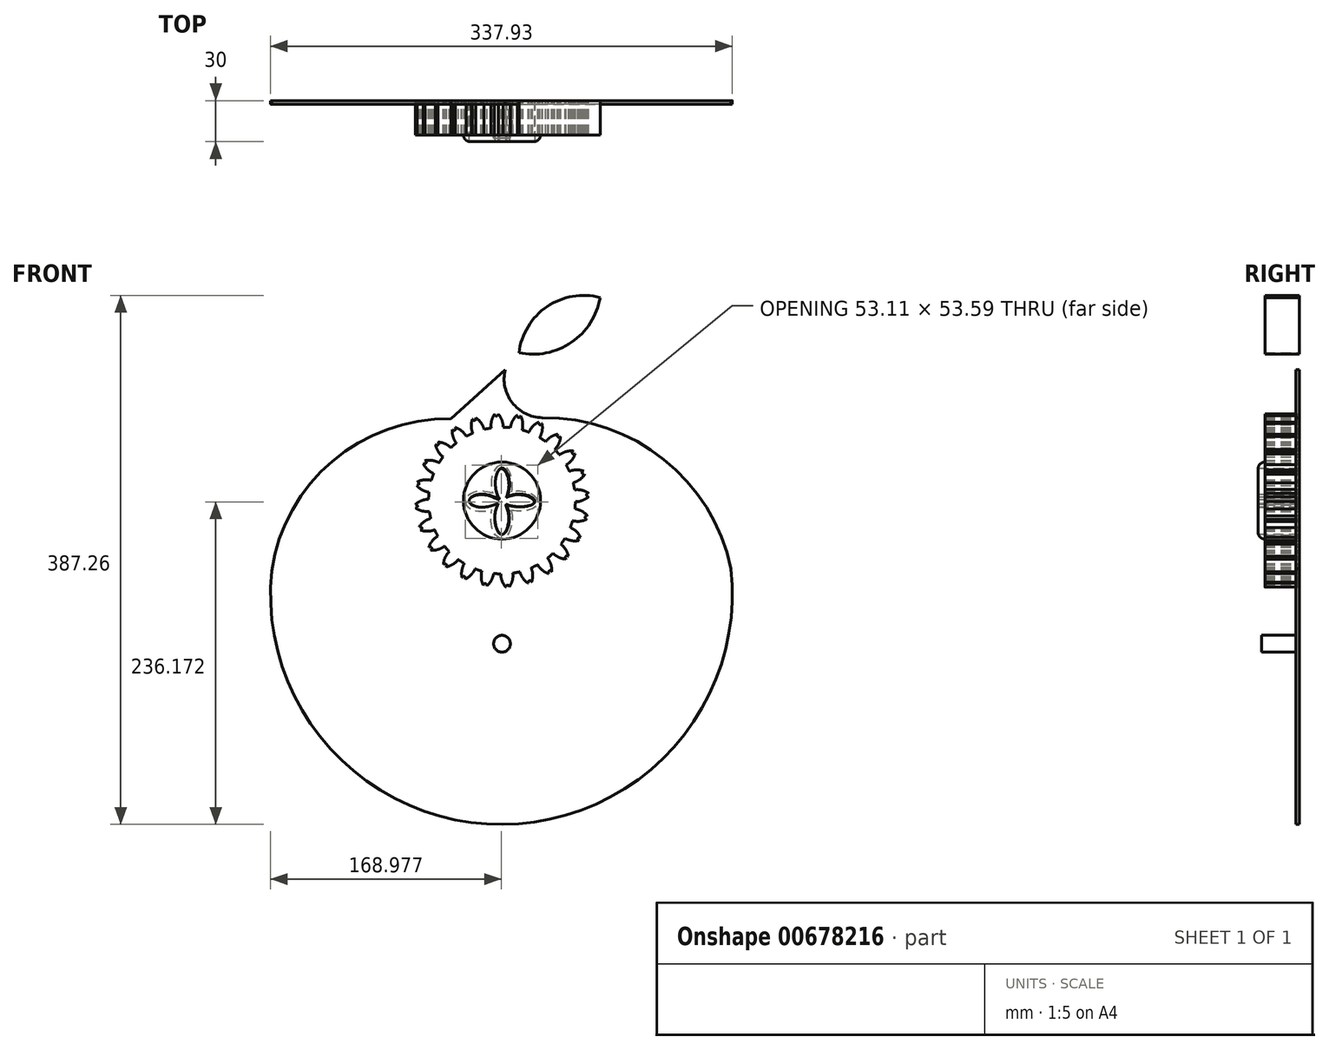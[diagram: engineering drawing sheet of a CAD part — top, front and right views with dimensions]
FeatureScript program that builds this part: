
annotation { "Feature Type Name" : "Feature", "Feature Type Description" : "" }
export const myFeature = defineFeature(function(context is Context, id is Id, definition is map)
    precondition{}
    {
        {
            var Q0;
            Q0=qCreatedBy(makeId("Front.planeOp"),FACE);
            var sketch = newSketch(context, id + "F0", { "sketchPlane" : qUnion([Q0])});
            skCircle(sketch, "E0", {"center": v(0, 0) * mm, "radius": 53.72 * mm});
            skCircle(sketch, "E1", {"center": v(0, 0) * mm, "radius": 58.67 * mm, "construction": true});
            skCircle(sketch, "E2", {"center": v(0, 0) * mm, "radius": 63.5 * mm, "construction": true});
            skLineSegment(sketch, "E3", {"start": v(0, 0) * mm, "end": v(0, 79.57) * mm, "construction": true});
            skLineSegment(sketch, "E4", {"start": v(0, 0) * mm, "end": v(-6.56, 100.09) * mm, "construction": true});
            skLineSegment(sketch, "E5", {"start": v(0, 58.67) * mm, "end": v(-52.8, 58.67) * mm, "construction": true});
            skLineSegment(sketch, "E6", {"start": v(0, 58.67) * mm, "end": v(-50.4, 40.33) * mm, "construction": true});
            skCircle(sketch, "E7", {"center": v(0, 0) * mm, "radius": 55.14 * mm, "construction": true});
            skCircle(sketch, "E8", {"center": v(0, 58.67) * mm, "radius": 14.6 * mm, "construction": true});
            skCircle(sketch, "E9", {"center": v(-13.72, 53.68) * mm, "radius": 14.6 * mm, "construction": true});
            skArc(sketch, "E10", {"start": v(0, 58.67) * mm, "mid": v(-1.2, 61.2) * mm, "end": v(-2.86, 63.44) * mm});
            skArc(sketch, "E11", {"start": v(0.88, 53.71) * mm, "mid": v(0.65, 56.23) * mm, "end": v(0, 58.67) * mm});
            skArc(sketch, "E12.MirrorCS", {"start": v(-7.66, 58.17) * mm, "mid": v(-6.8, 60.83) * mm, "end": v(-5.45, 63.27) * mm});
            skArc(sketch, "E13.MirrorCS", {"start": v(-7.88, 53.14) * mm, "mid": v(-7.99, 55.67) * mm, "end": v(-7.66, 58.17) * mm});
            skArc(sketch, "E14", {"start": v(-5.45, 63.27) * mm, "mid": v(-4.06, 61.88) * mm, "end": v(-2.86, 63.44) * mm});
            skCircle(sketch, "E15", {"center": v(0, 0) * mm, "radius": 28.21 * mm});
            skFitSpline(sketch, "E16", {"points": [v(0.41, -0.45) * mm, v(0, 0) * mm, v(-14.37, 4.8) * mm, v(-24, 0) * mm, v(-14.67, -4.85) * mm, v(0.41, -0.45) * mm]});
            skFitSpline(sketch, "E17", {"points": [v(0.41, -0.45) * mm, v(14.8, -4.52) * mm, v(24.13, -0.45) * mm, v(13.08, 4.76) * mm, v(0.41, -0.45) * mm]});
            skFitSpline(sketch, "E18", {"points": [v(0.41, -0.45) * mm, v(5.53, 12.84) * mm, v(0, 23.86) * mm, v(-4.88, 13.02) * mm, v(0.41, -0.45) * mm]});
            skFitSpline(sketch, "E19", {"points": [v(0, 0) * mm, v(5.4, -13.04) * mm, v(0, -24.75) * mm, v(-5.25, -13.1) * mm, v(0, 0) * mm]});
            skSolve(sketch);
        }
        {
            var Q0;
            {var subQ0=sQuery(id+"F0.wireOp",EDGE,"E0");var subQ1=makeQuery(id+"F0.imprint","INTERSECT",VERTEX,{"derivedFrom":[subQ0,sQuery(id+"F0.wireOp",EDGE,"E11")]});Q0=makeQuery(id+"F0.imprint","IMPRINT",FACE,{"disambiguationData":[TD([[makeQuery(id+"F0.imprint","IMPRINT",EDGE,{"disambiguationData":[TD([[subQ1,-1.0]])],"derivedFrom":subQ0}),1.0]])]});}
            var Q1;
            Q1=makeQuery(id+"F0.imprint","IMPRINT",FACE,{"disambiguationData":[TD([[makeQuery(id+"F0.imprint","IMPRINT",EDGE,{"derivedFrom":sQuery(id+"F0.wireOp",EDGE,"E10")}),1.0]])]});
            extrude(context, id + "F1", {"entities" : qUnion([Q0, Q1]), "depth" : 25 * mm, "offsetDistance" : 25 * mm});
        }
        {
            var Q0;
            Q0=makeQuery(id+"F1.opExtrude","SWEPT_BODY",BODY,{"disambiguationData":[OSD([sQuery(id+"F0.wireOp",EDGE,"E0"),sQuery(id+"F0.wireOp",EDGE,"E10"),sQuery(id+"F0.wireOp",EDGE,"E11"),sQuery(id+"F0.wireOp",EDGE,"E12.MirrorCS"),sQuery(id+"F0.wireOp",EDGE,"E13.MirrorCS"),sQuery(id+"F0.wireOp",EDGE,"E14")])]});
            var Q1;
            Q1=makeQuery(id+"F1.opExtrude","SWEPT_FACE",FACE,{"disambiguationData":[OSD([sQuery(id+"F0.wireOp",EDGE,"E0")])]});
            circularPattern(context, id + "F2", {"entities" : qUnion([Q0]), "axis" : qUnion([Q1]), "angle" : 360 * degree, "instanceCount" : 24, "equalSpace" : true});
        }
        {
            var Q0;
            Q0=makeQuery(id+"F0.imprint","IMPRINT",FACE,{"disambiguationData":[TD([[makeQuery(id+"F0.imprint","IMPRINT",EDGE,{"derivedFrom":sQuery(id+"F0.wireOp",EDGE,"E15")}),1.0]])]});
            extrude(context, id + "F3", {"entities" : qUnion([Q0]), "operationType" : NewBodyOperationType.ADD, "depth" : 30 * mm, "offsetDistance" : 25 * mm});
        }
        {
            var Q0;
            Q0=makeQuery(id+"F3.opExtrude","CAP_EDGE",EDGE,{"disambiguationData":[OSD([sQuery(id+"F0.wireOp",EDGE,"E15")])],"isStart":false});
            fillet(context, id + "F4", {"entities" : qUnion([Q0]), "radius" : 5 * mm, "tangentPropagation" : true, "allowEdgeOverflow" : false});
        }
        {
            var Q0;
            Q0=qCreatedBy(makeId("Front.planeOp"),FACE);
            var sketch = newSketch(context, id + "F5", { "sketchPlane" : qUnion([Q0])});
            skArc(sketch, "E20", {"start": v(-171.04, -51.27) * mm, "mid": v(0.49, -239.58) * mm, "end": v(170.05, -49.5) * mm});
            skArc(sketch, "E21", {"start": v(-38.25, 62.35) * mm, "mid": v(-125.97, 30.46) * mm, "end": v(-171.04, -51.27) * mm});
            skArc(sketch, "E22", {"start": v(170.05, -49.5) * mm, "mid": v(119.95, 32.07) * mm, "end": v(29.42, 63.16) * mm});
            skFitSpline(sketch, "E23", {"points": [v(-0.05, -0.9) * mm, v(-0.47, -0.45) * mm, v(-14.84, 4.34) * mm, v(-24.46, -0.45) * mm, v(-15.13, -5.3) * mm, v(-0.05, -0.9) * mm]});
            skFitSpline(sketch, "E24", {"points": [v(-0.05, -0.9) * mm, v(14.33, -4.97) * mm, v(23.66, -0.9) * mm, v(12.61, 4.3) * mm, v(-0.05, -0.9) * mm]});
            skFitSpline(sketch, "E25", {"points": [v(-0.05, -0.9) * mm, v(5.06, 12.39) * mm, v(-0.47, 23.4) * mm, v(-5.35, 12.57) * mm, v(-0.05, -0.9) * mm]});
            skFitSpline(sketch, "E26", {"points": [v(-0.47, -0.45) * mm, v(4.94, -13.5) * mm, v(-0.47, -25.2) * mm, v(-5.72, -13.56) * mm, v(-0.47, -0.45) * mm]});
            skArc(sketch, "E27", {"start": v(12.44, 108.19) * mm, "mid": v(5.71, 79.94) * mm, "end": v(29.42, 63.16) * mm});
            skArc(sketch, "E28", {"start": v(71.9, 148.64) * mm, "mid": v(32.98, 141.92) * mm, "end": v(12.44, 108.19) * mm});
            skArc(sketch, "E29", {"start": v(12.44, 108.19) * mm, "mid": v(50.78, 115.75) * mm, "end": v(71.9, 148.64) * mm});
            skLineSegment(sketch, "E30", {"start": v(12.44, 108.19) * mm, "end": v(-38.25, 62.35) * mm});
            skSolve(sketch);
        }
        {
            var Q0;
            Q0=makeQuery(id+"F5.imprint","IMPRINT",FACE,{"disambiguationData":[TD([[makeQuery(id+"F5.imprint","IMPRINT",EDGE,{"derivedFrom":sQuery(id+"F5.wireOp",EDGE,"E20")}),1.0]])]});
            extrude(context, id + "F6", {"entities" : qUnion([Q0]), "depth" : 25 * mm, "offsetDistance" : 25 * mm});
        }
        {
            var Q0;
            Q0=makeQuery(id+"F5.imprint","IMPRINT",FACE,{"disambiguationData":[TD([[makeQuery(id+"F5.imprint","IMPRINT",EDGE,{"derivedFrom":sQuery(id+"F5.wireOp",EDGE,"E28")}),1.0]])]});
            extrude(context, id + "F7", {"entities" : qUnion([Q0]), "depth" : 25 * mm, "offsetDistance" : 25 * mm});
        }
        {
            var Q0;
            Q0=makeQuery(id+"F6.opExtrude","CAP_FACE",FACE,{"disambiguationData":[OSD([sQuery(id+"F5.wireOp",EDGE,"E20"),sQuery(id+"F5.wireOp",EDGE,"E21"),sQuery(id+"F5.wireOp",EDGE,"E22"),sQuery(id+"F5.wireOp",EDGE,"E23"),sQuery(id+"F5.wireOp",EDGE,"E24"),sQuery(id+"F5.wireOp",EDGE,"E25"),sQuery(id+"F5.wireOp",EDGE,"E26"),sQuery(id+"F5.wireOp",EDGE,"E27"),sQuery(id+"F5.wireOp",EDGE,"E30")])],"isStart":false});
            shell(context, id + "F8", {"entities" : qUnion([Q0]), "thickness" : 2.5 * mm});
        }
        {
            var Q0;
            Q0=makeQuery(id+"F6.opExtrude","CAP_FACE",FACE,{"disambiguationData":[OSD([sQuery(id+"F5.wireOp",EDGE,"E20"),sQuery(id+"F5.wireOp",EDGE,"E21"),sQuery(id+"F5.wireOp",EDGE,"E22"),sQuery(id+"F5.wireOp",EDGE,"E23"),sQuery(id+"F5.wireOp",EDGE,"E24"),sQuery(id+"F5.wireOp",EDGE,"E25"),sQuery(id+"F5.wireOp",EDGE,"E26"),sQuery(id+"F5.wireOp",EDGE,"E27"),sQuery(id+"F5.wireOp",EDGE,"E30")])],"isStart":false});
            extrude(context, id + "F9", {"entities" : qUnion([Q0]), "operationType" : NewBodyOperationType.REMOVE, "oppositeDirection" : true, "depth" : 25 * mm, "offsetDistance" : 25 * mm});
        }
        {
            var Q0;
            {var subQ0=sQuery(id+"F5.wireOp",EDGE,"E30");var subQ1=sQuery(id+"F5.wireOp",EDGE,"E27");var subQ2=sQuery(id+"F5.wireOp",EDGE,"E26");var subQ3=sQuery(id+"F5.wireOp",EDGE,"E25");var subQ4=sQuery(id+"F5.wireOp",EDGE,"E24");var subQ5=sQuery(id+"F5.wireOp",EDGE,"E23");var subQ6=sQuery(id+"F5.wireOp",EDGE,"E22");var subQ7=sQuery(id+"F5.wireOp",EDGE,"E21");var subQ8=sQuery(id+"F5.wireOp",EDGE,"E20");Q0=makeQuery(id+"F8.opShell","OFFSET_FACE",FACE,{"disambiguationData":[OSD([subQ8,subQ7,subQ6,subQ5,subQ4,subQ3,subQ2,subQ1,subQ0]),TDD([makeQuery(id+"F6.opExtrude","CAP_FACE",FACE,{"disambiguationData":[OSD([subQ8,subQ7,subQ6,subQ5,subQ4,subQ3,subQ2,subQ1,subQ0])],"isStart":true})])]});}
            var sketch = newSketch(context, id + "F10", { "sketchPlane" : qUnion([Q0])});
            skCircle(sketch, "E31", {"center": v(0, -104.8) * mm, "radius": 6.15 * mm});
            skSolve(sketch);
        }
        {
            var Q0;
            Q0=makeQuery(id+"F10.imprint","IMPRINT",FACE,{"disambiguationData":[TD([[makeQuery(id+"F10.imprint","IMPRINT",EDGE,{"derivedFrom":sQuery(id+"F10.wireOp",EDGE,"E31")}),1.0]])]});
            var Q1;
            Q1=sQuery(id+"F10.wireOp",EDGE,"E31");
            extrude(context, id + "F11", {"entities" : qUnion([Q0]), "operationType" : NewBodyOperationType.ADD, "surfaceOperationType" : NewSurfaceOperationType.ADD, "surfaceEntities" : qUnion([Q1]), "depth" : 25 * mm, "offsetDistance" : 25 * mm});
        }
    });
